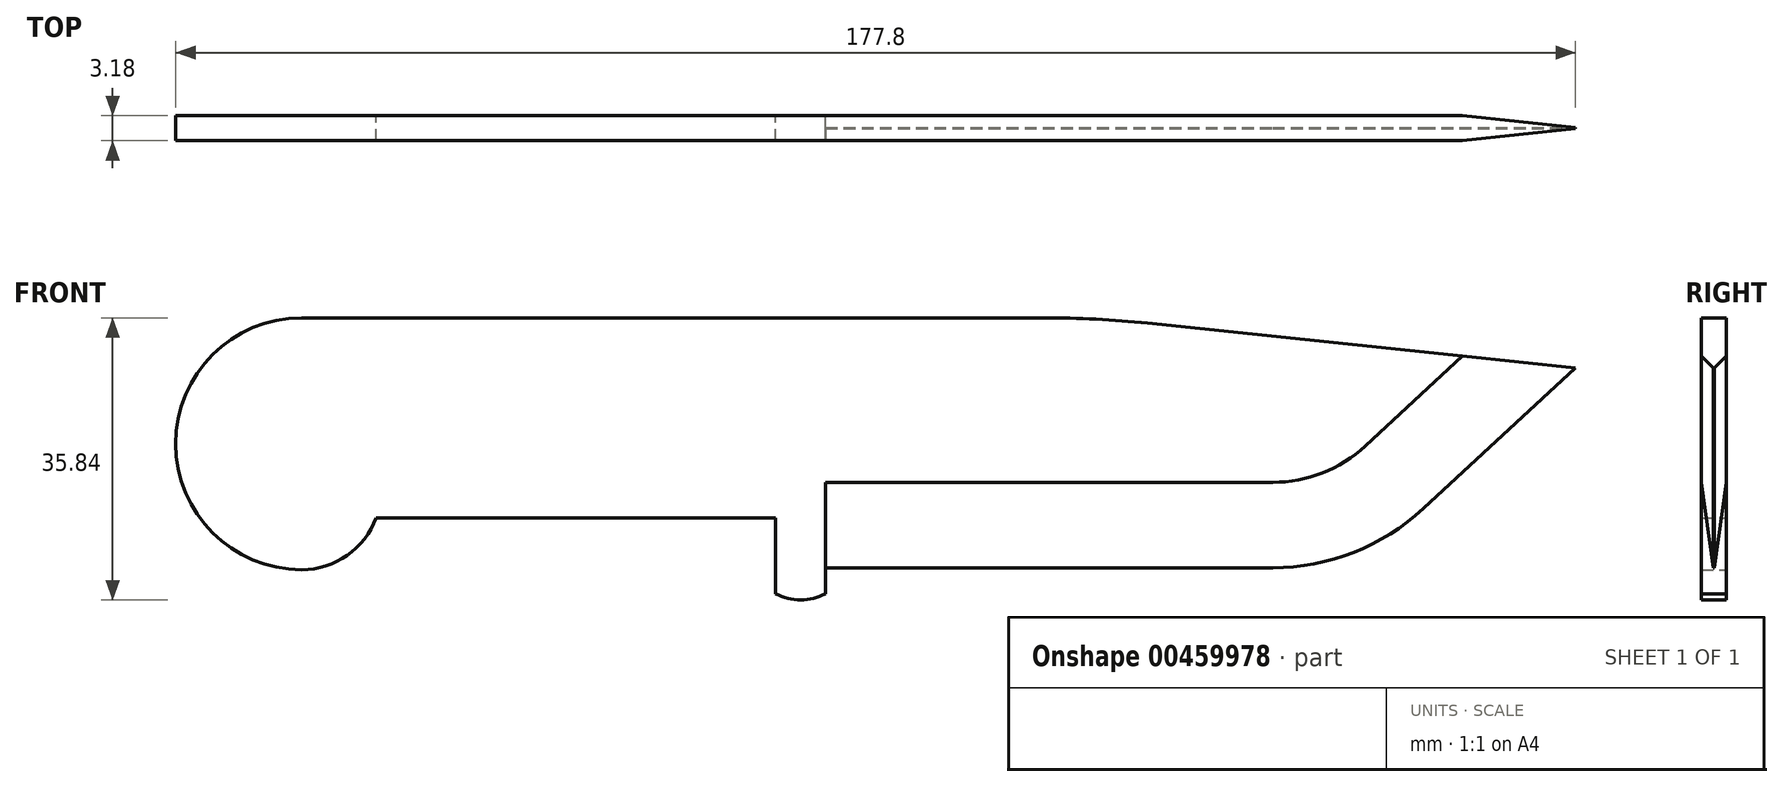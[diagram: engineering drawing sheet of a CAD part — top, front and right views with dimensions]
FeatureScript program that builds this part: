
annotation { "Feature Type Name" : "Feature", "Feature Type Description" : "" }
export const myFeature = defineFeature(function(context is Context, id is Id, definition is map)
    precondition{}
    {
        {
            var Q0;
            Q0=qCreatedBy(makeId("Front.planeOp"),FACE);
            var sketch = newSketch(context, id + "F0", { "sketchPlane" : qUnion([Q0])});
            skLineSegment(sketch, "E0", {"start": v(0, 0) * mm, "end": v(94.28, 0) * mm});
            skArc(sketch, "E1", {"start": v(0, 0) * mm, "mid": v(-16, -16) * mm, "end": v(0, -32) * mm});
            skArc(sketch, "E2", {"start": v(0, -32) * mm, "mid": v(5.77, -30.19) * mm, "end": v(9.46, -25.4) * mm});
            skLineSegment(sketch, "E3", {"start": v(9.46, -25.4) * mm, "end": v(60.2, -25.4) * mm});
            skLineSegment(sketch, "E4", {"start": v(60.2, -25.4) * mm, "end": v(60.2, -35.05) * mm});
            skArc(sketch, "E5", {"start": v(60.2, -35.05) * mm, "mid": v(63.37, -35.84) * mm, "end": v(66.55, -35.05) * mm});
            skLineSegment(sketch, "E6", {"start": v(66.55, -35.05) * mm, "end": v(66.55, -31.75) * mm});
            skLineSegment(sketch, "E7", {"start": v(66.55, -31.75) * mm, "end": v(123.36, -31.75) * mm});
            skPoint(sketch, "E8", {"position": v(-16, -16) * mm});
            skArc(sketch, "E9", {"start": v(123.36, -31.75) * mm, "mid": v(133.63, -29.8) * mm, "end": v(142.48, -24.25) * mm});
            skLineSegment(sketch, "E10", {"start": v(142.48, -24.25) * mm, "end": v(161.8, -6.35) * mm});
            skLineSegment(sketch, "E11", {"start": v(107.45, -0.68) * mm, "end": v(161.8, -6.35) * mm});
            skPoint(sketch, "E12.visualSharp", {"position": v(100.88, 0) * mm});
            skArc(sketch, "E12.filletArc", {"start": v(107.45, -0.68) * mm, "mid": v(100.87, -0.17) * mm, "end": v(94.28, 0) * mm});
            skSolve(sketch);
        }
        {
            var Q0;
            Q0 = qSketchRegion(id + "F0", true);
            extrude(context, id + "F1", {"entities" : qUnion([Q0]), "depth" : 3.17 * mm});
        }
        {
            var Q0;
            Q0=makeQuery(id+"F1.opExtrude","SWEPT_FACE",FACE,{"disambiguationData":[OSD([sQuery(id+"F0.wireOp",EDGE,"E6")])]});
            var sketch = newSketch(context, id + "F2", { "sketchPlane" : qUnion([Q0])});
            skLineSegment(sketch, "E13", {"start": v(-1.65, -31.75) * mm, "end": v(-3.18, -20.9) * mm});
            skLineSegment(sketch, "E14", {"start": v(-3.18, -20.9) * mm, "end": v(-3.18, -31.75) * mm});
            skLineSegment(sketch, "E15", {"start": v(-3.18, -31.75) * mm, "end": v(-1.65, -31.75) * mm});
            skSolve(sketch);
        }
        {
            var Q0;
            Q0 = qSketchRegion(id + "F2", true);
            var Q1;
            Q1=makeQuery(id+"F1.opExtrude","CAP_EDGE",EDGE,{"disambiguationData":[OSD([sQuery(id+"F0.wireOp",EDGE,"E7")])],"isStart":false});
            var Q2;
            Q2=makeQuery(id+"F1.opExtrude","CAP_EDGE",EDGE,{"disambiguationData":[OSD([sQuery(id+"F0.wireOp",EDGE,"E9")])],"isStart":false});
            var Q3;
            Q3=makeQuery(id+"F1.opExtrude","CAP_EDGE",EDGE,{"disambiguationData":[OSD([sQuery(id+"F0.wireOp",EDGE,"E10")])],"isStart":false});
            sweep(context, id + "F3", {"operationType" : NewBodyOperationType.REMOVE, "profiles" : qUnion([Q0]), "path" : qUnion([Q1, Q2, Q3])});
        }
        {
            var Q0;
            {var subQ0=sQuery(id+"F0.wireOp",EDGE,"E6");Q0=makeQuery(id+"F3.boolean.opBoolean","MERGE",FACE,{"derivedFrom":[makeQuery(id+"F1.opExtrude","SWEPT_FACE",FACE,{"disambiguationData":[OSD([subQ0])]}),makeQuery(id+"F3.opSweep","CAP_FACE",FACE,{"disambiguationData":[OSD([subQ0,sQuery(id+"F0.wireOp",EDGE,"E7"),sQuery(id+"F2.wireOp",EDGE,"E13"),sQuery(id+"F2.wireOp",EDGE,"E14"),sQuery(id+"F2.wireOp",EDGE,"E15")])],"isStart":true})]});}
            var sketch = newSketch(context, id + "F4", { "sketchPlane" : qUnion([Q0])});
            skLineSegment(sketch, "E16", {"start": v(-1.52, -31.75) * mm, "end": v(0, -20.9) * mm});
            skLineSegment(sketch, "E17", {"start": v(0, -20.9) * mm, "end": v(0, -31.75) * mm});
            skLineSegment(sketch, "E18", {"start": v(0, -31.75) * mm, "end": v(-1.52, -31.75) * mm});
            skSolve(sketch);
        }
        {
            var Q0;
            Q0 = qSketchRegion(id + "F4", true);
            var Q1;
            Q1=makeQuery(id+"F1.opExtrude","CAP_EDGE",EDGE,{"disambiguationData":[OSD([sQuery(id+"F0.wireOp",EDGE,"E7")])],"isStart":true});
            var Q2;
            Q2=makeQuery(id+"F1.opExtrude","CAP_EDGE",EDGE,{"disambiguationData":[OSD([sQuery(id+"F0.wireOp",EDGE,"E9")])],"isStart":true});
            var Q3;
            Q3=makeQuery(id+"F1.opExtrude","CAP_EDGE",EDGE,{"disambiguationData":[OSD([sQuery(id+"F0.wireOp",EDGE,"E10")])],"isStart":true});
            sweep(context, id + "F5", {"operationType" : NewBodyOperationType.REMOVE, "profiles" : qUnion([Q0]), "path" : qUnion([Q1, Q2, Q3])});
        }
    });
